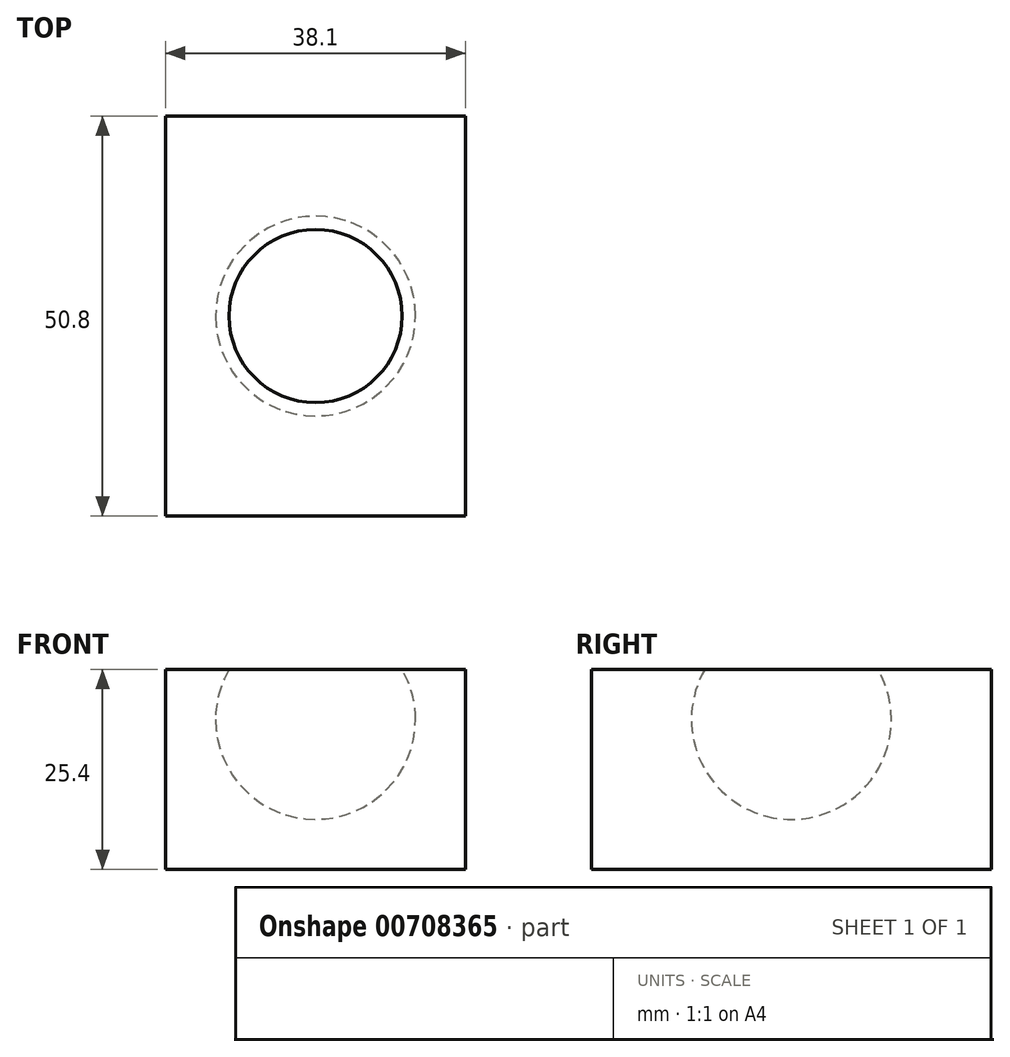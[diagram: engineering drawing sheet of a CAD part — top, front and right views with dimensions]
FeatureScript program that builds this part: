
annotation { "Feature Type Name" : "Feature", "Feature Type Description" : "" }
export const myFeature = defineFeature(function(context is Context, id is Id, definition is map)
    precondition{}
    {
        {
            var Q0;
            Q0=qCreatedBy(makeId("Top.planeOp"),FACE);
            var sketch = newSketch(context, id + "F0", { "sketchPlane" : qUnion([Q0])});
            skLineSegment(sketch, "E0.bottom", {"start": v(19.05, 25.4) * mm, "end": v(-19.05, 25.4) * mm});
            skLineSegment(sketch, "E0.top", {"start": v(19.05, -25.4) * mm, "end": v(-19.05, -25.4) * mm});
            skLineSegment(sketch, "E0.left", {"start": v(19.05, 25.4) * mm, "end": v(19.05, -25.4) * mm});
            skLineSegment(sketch, "E0.right", {"start": v(-19.05, 25.4) * mm, "end": v(-19.05, -25.4) * mm});
            skPoint(sketch, "E0.middle", {"position": v(0, 0) * mm});
            skSolve(sketch);
        }
        {
            var Q0;
            Q0 = qSketchRegion(id + "F0", true);
            extrude(context, id + "F1", {"entities" : qUnion([Q0]), "depth" : 25.4 * mm, "offsetDistance" : 25.4 * mm});
        }
        {
            var Q0;
            Q0=makeQuery(id+"F1.opExtrude","CAP_FACE",FACE,{"disambiguationData":[OSD([sQuery(id+"F0.wireOp",EDGE,"E0.bottom"),sQuery(id+"F0.wireOp",EDGE,"E0.top"),sQuery(id+"F0.wireOp",EDGE,"E0.left"),sQuery(id+"F0.wireOp",EDGE,"E0.right")])],"isStart":false});
            cPlane(context, id + "F2", {"entities" : qUnion([Q0]), "cplaneType" : CPlaneType.OFFSET, "offset" : 6.35 * mm, "oppositeDirection" : true, "width" : 152.4 * mm, "height" : 152.4 * mm});
        }
        {
            var Q0;
            Q0=qCreatedBy(id+"F2.planeOp",FACE);
            var sketch = newSketch(context, id + "F3", { "sketchPlane" : qUnion([Q0])});
            skArc(sketch, "E1", {"start": v(12.7, 0) * mm, "mid": v(0, -12.7) * mm, "end": v(-12.7, 0) * mm});
            skLineSegment(sketch, "E2", {"start": v(-12.7, 0) * mm, "end": v(12.7, 0) * mm});
            skSolve(sketch);
        }
        {
            var Q0;
            Q0 = qSketchRegion(id + "F3", true);
            var Q1;
            Q1=sQuery(id+"F3.wireOp",EDGE,"E2");
            revolve(context, id + "F4", {"operationType" : NewBodyOperationType.REMOVE, "surfaceOperationType" : NewSurfaceOperationType.NEW, "entities" : qUnion([Q0]), "axis" : qUnion([Q1]), "revolveType" : RevolveType.FULL, "oppositeDirection" : true});
        }
    });
